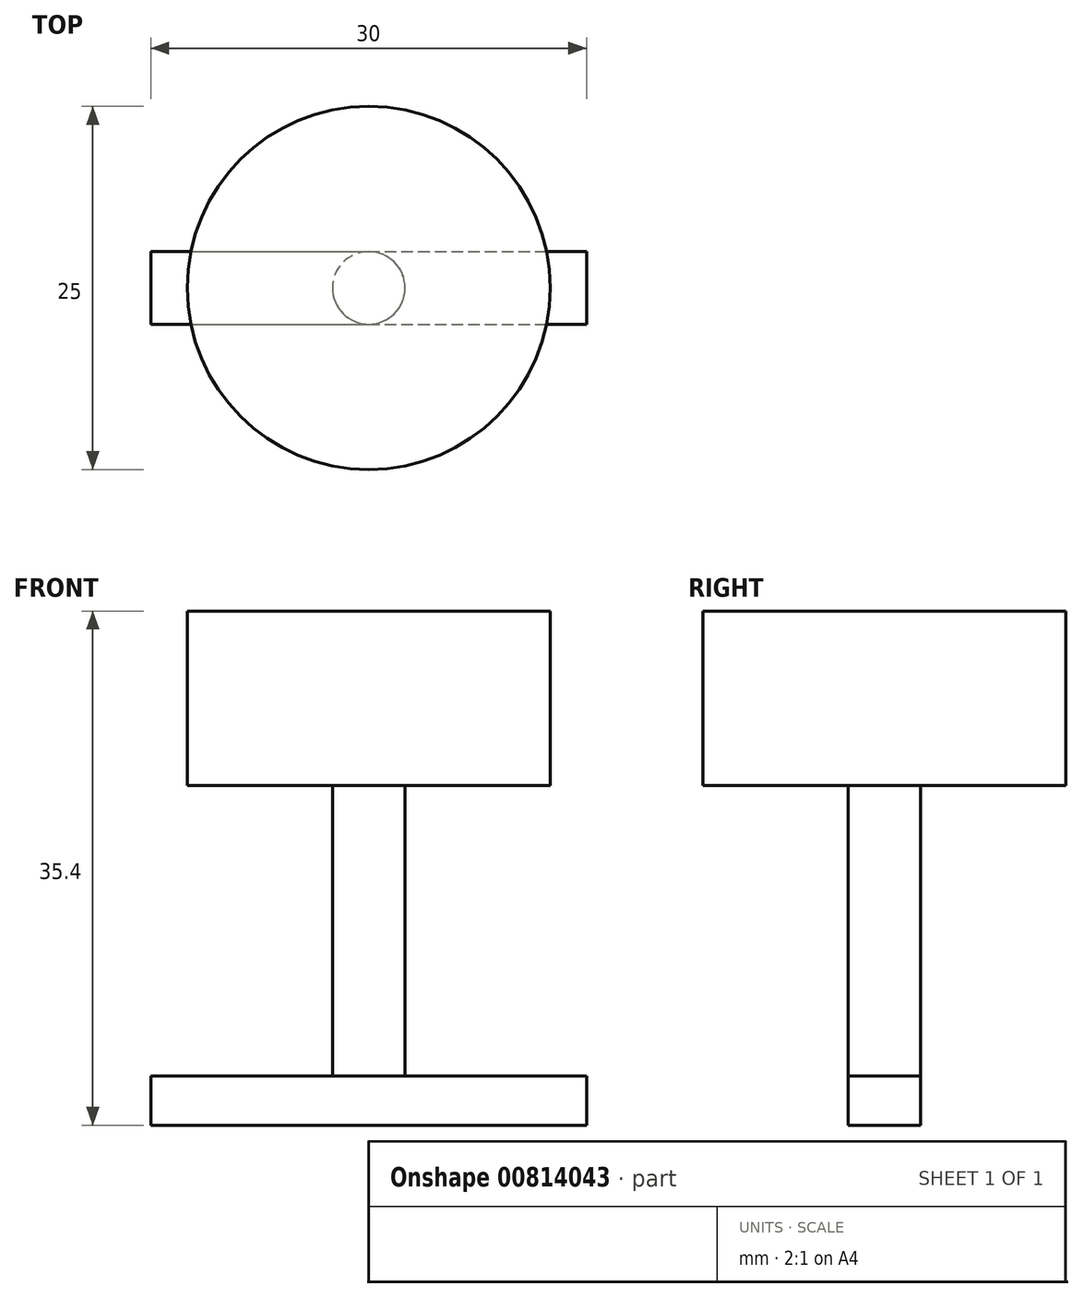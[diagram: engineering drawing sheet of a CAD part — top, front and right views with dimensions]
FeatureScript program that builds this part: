
annotation { "Feature Type Name" : "Feature", "Feature Type Description" : "" }
export const myFeature = defineFeature(function(context is Context, id is Id, definition is map)
    precondition{}
    {
        {
            var Q0;
            Q0=qCreatedBy(makeId("Top.planeOp"),FACE);
            var sketch = newSketch(context, id + "F0", { "sketchPlane" : qUnion([Q0])});
            skCircle(sketch, "E0", {"center": v(0, 0) * mm, "radius": 12.5 * mm});
            skSolve(sketch);
        }
        {
            var Q0;
            Q0 = qSketchRegion(id + "F0", true);
            extrude(context, id + "F1", {"entities" : qUnion([Q0]), "depth" : 12 * mm, "offsetDistance" : 25 * mm});
        }
        {
            var Q0;
            Q0=makeQuery(id+"F1.opExtrude","CAP_FACE",FACE,{"disambiguationData":[OSD([sQuery(id+"F0.wireOp",EDGE,"E0")])],"isStart":true});
            var sketch = newSketch(context, id + "F2", { "sketchPlane" : qUnion([Q0])});
            skCircle(sketch, "E1", {"center": v(0, 0) * mm, "radius": 2.5 * mm});
            skSolve(sketch);
        }
        {
            var Q0;
            Q0 = qSketchRegion(id + "F2", true);
            extrude(context, id + "F3", {"entities" : qUnion([Q0]), "operationType" : NewBodyOperationType.ADD, "depth" : 20 * mm, "offsetDistance" : 25 * mm});
        }
        {
            var Q0;
            Q0=makeQuery(id+"F3.opExtrude","CAP_FACE",FACE,{"disambiguationData":[OSD([sQuery(id+"F2.wireOp",EDGE,"E1")])],"isStart":false});
            var sketch = newSketch(context, id + "F4", { "sketchPlane" : qUnion([Q0])});
            skLineSegment(sketch, "E2.bottom", {"start": v(-15, 2.5) * mm, "end": v(15, 2.5) * mm});
            skLineSegment(sketch, "E2.top", {"start": v(-15, -2.5) * mm, "end": v(15, -2.5) * mm});
            skLineSegment(sketch, "E2.left", {"start": v(-15, 2.5) * mm, "end": v(-15, -2.5) * mm});
            skLineSegment(sketch, "E2.right", {"start": v(15, 2.5) * mm, "end": v(15, -2.5) * mm});
            skPoint(sketch, "E2.middle", {"position": v(0, 0) * mm});
            skSolve(sketch);
        }
        {
            var Q0;
            Q0 = qSketchRegion(id + "F4", true);
            extrude(context, id + "F5", {"entities" : qUnion([Q0]), "operationType" : NewBodyOperationType.ADD, "depth" : 3.4 * mm, "offsetDistance" : 25 * mm});
        }
    });
